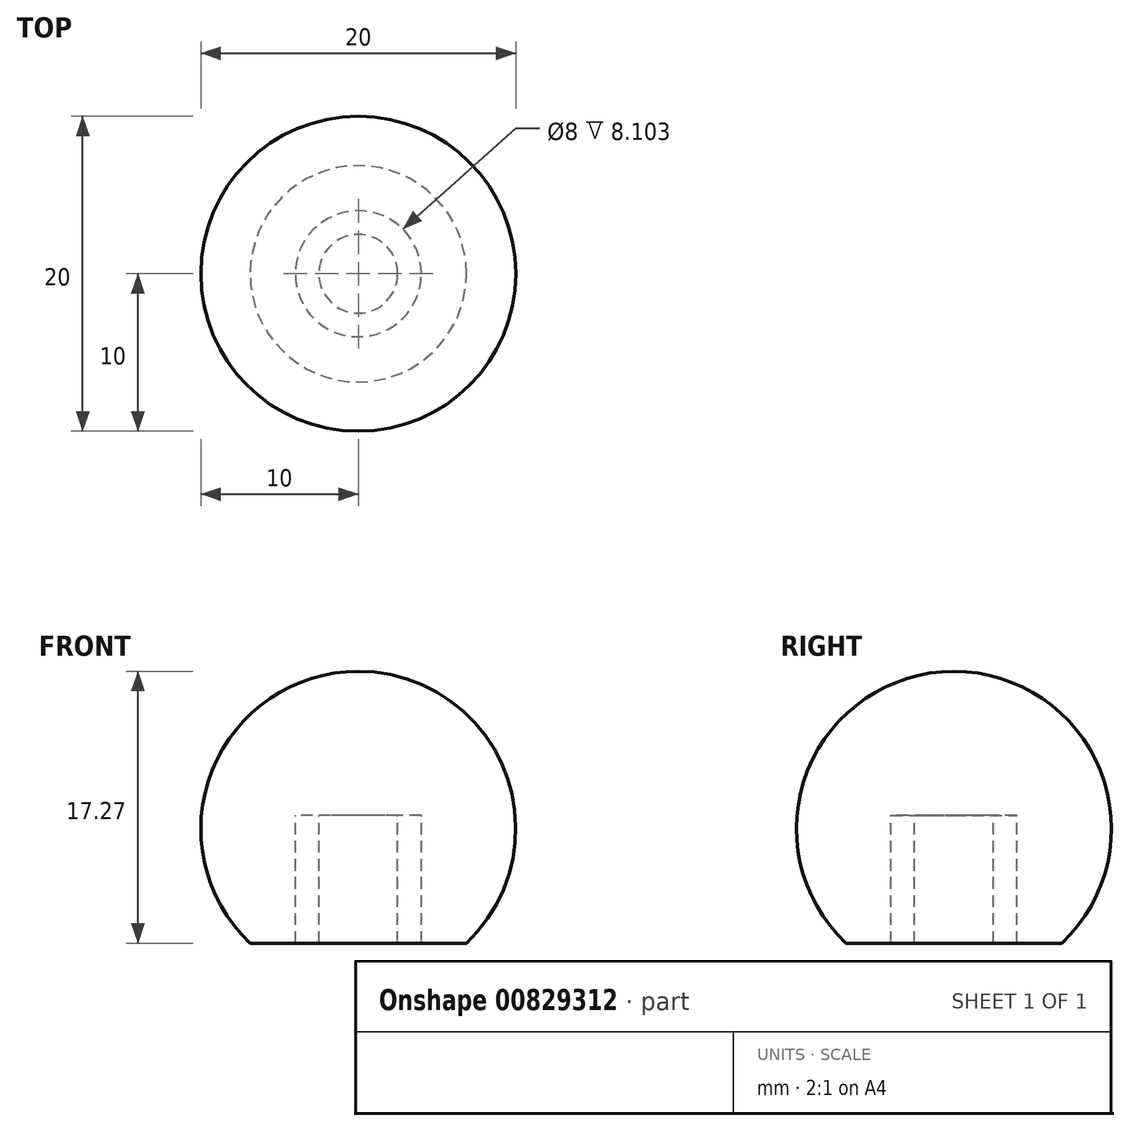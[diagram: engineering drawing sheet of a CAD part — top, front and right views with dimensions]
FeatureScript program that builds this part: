
annotation { "Feature Type Name" : "Feature", "Feature Type Description" : "" }
export const myFeature = defineFeature(function(context is Context, id is Id, definition is map)
    precondition{}
    {
        {
            var Q0;
            Q0=qCreatedBy(makeId("Front.planeOp"),FACE);
            var sketch = newSketch(context, id + "F0", { "sketchPlane" : qUnion([Q0])});
            skArc(sketch, "E0", {"start": v(0, 10) * mm, "mid": v(-9.3, 3.7) * mm, "end": v(-6.87, -7.27) * mm});
            skLineSegment(sketch, "E1", {"start": v(-2.5, 0.83) * mm, "end": v(-4, 0.83) * mm});
            skLineSegment(sketch, "E2", {"start": v(-4, 0.83) * mm, "end": v(-4, -7.27) * mm});
            skLineSegment(sketch, "E3", {"start": v(0, 10) * mm, "end": v(0, 0.83) * mm});
            skLineSegment(sketch, "E4", {"start": v(0, -7.27) * mm, "end": v(-2.5, -7.27) * mm, "construction": true});
            skLineSegment(sketch, "E5", {"start": v(-2.5, -7.27) * mm, "end": v(-2.5, 0.83) * mm});
            skLineSegment(sketch, "E6", {"start": v(-2.5, -7.27) * mm, "end": v(0, -7.27) * mm});
            skLineSegment(sketch, "E7", {"start": v(0, 0.83) * mm, "end": v(0, -7.27) * mm});
            skLineSegment(sketch, "E8", {"start": v(-4, -7.27) * mm, "end": v(-6.87, -7.27) * mm});
            skSolve(sketch);
        }
        {
            var Q0;
            Q0=makeQuery(id+"F0.imprint","IMPRINT",FACE,{"disambiguationData":[TD([[makeQuery(id+"F0.imprint","IMPRINT",EDGE,{"derivedFrom":sQuery(id+"F0.wireOp",EDGE,"E0")}),1.0]])]});
            var Q1;
            Q1=sQuery(id+"F0.wireOp",EDGE,"E3");
            revolve(context, id + "F1", {"surfaceOperationType" : NewSurfaceOperationType.NEW, "entities" : qUnion([Q0]), "axis" : qUnion([Q1]), "revolveType" : RevolveType.FULL});
        }
    });
